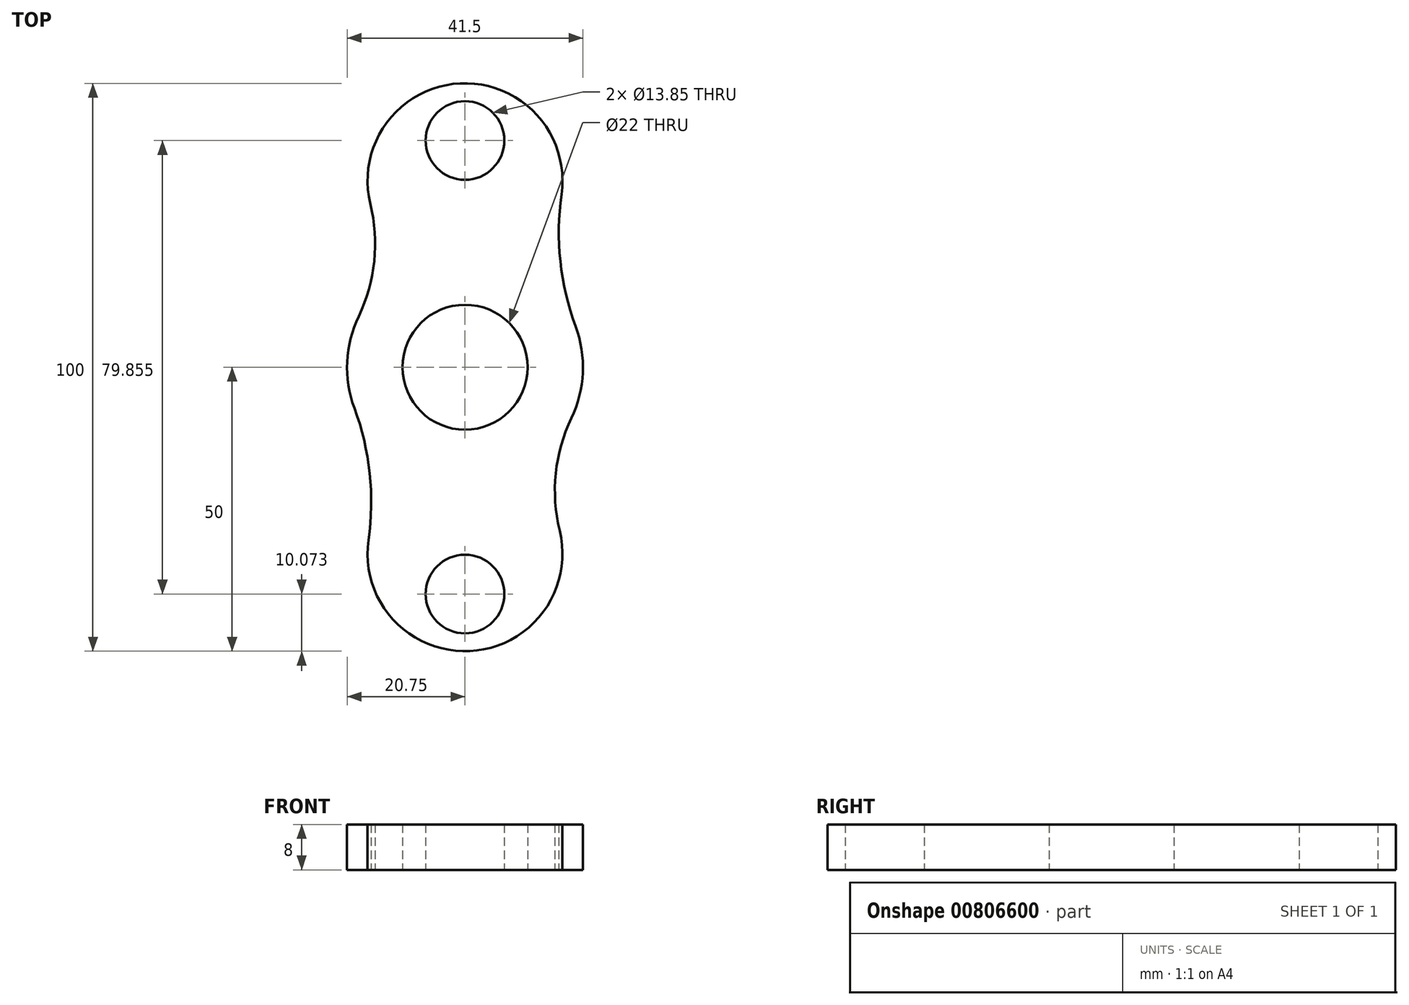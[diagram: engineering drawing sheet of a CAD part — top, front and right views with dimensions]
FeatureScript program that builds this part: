
annotation { "Feature Type Name" : "Feature", "Feature Type Description" : "" }
export const myFeature = defineFeature(function(context is Context, id is Id, definition is map)
    precondition{}
    {
        {
            var Q0;
            Q0=qCreatedBy(makeId("Top.planeOp"),FACE);
            var sketch = newSketch(context, id + "F0", { "sketchPlane" : qUnion([Q0])});
            skCircle(sketch, "E0", {"center": v(0, 0) * mm, "radius": 11 * mm});
            skCircle(sketch, "E1", {"center": v(0, 0) * mm, "radius": 50 * mm, "construction": true});
            skArc(sketch, "E2", {"start": v(16.99, 30.43) * mm, "mid": v(-0.84, 49.98) * mm, "end": v(-16.67, 28.77) * mm});
            skArc(sketch, "E3", {"start": v(-18.72, 8.96) * mm, "mid": v(-20.73, 0.96) * mm, "end": v(-19.47, -7.2) * mm});
            skArc(sketch, "E4", {"start": v(-18.72, 8.96) * mm, "mid": v(-15.98, 18.69) * mm, "end": v(-16.67, 28.77) * mm});
            skArc(sketch, "E5", {"start": v(16.99, 30.43) * mm, "mid": v(16.78, 18.66) * mm, "end": v(19.47, 7.2) * mm});
            skArc(sketch, "E6.1.0", {"start": v(-16.99, -30.43) * mm, "mid": v(-16.78, -18.66) * mm, "end": v(-19.47, -7.2) * mm});
            skArc(sketch, "E6.1.1", {"start": v(-16.99, -30.43) * mm, "mid": v(0.84, -49.98) * mm, "end": v(16.67, -28.77) * mm});
            skArc(sketch, "E6.1.2", {"start": v(18.72, -8.96) * mm, "mid": v(15.98, -18.69) * mm, "end": v(16.67, -28.77) * mm});
            skArc(sketch, "E7.trimOffspring", {"start": v(18.72, -8.96) * mm, "mid": v(20.73, -0.96) * mm, "end": v(19.47, 7.2) * mm});
            skCircle(sketch, "E8", {"center": v(0, 39.93) * mm, "radius": 6.93 * mm});
            skCircle(sketch, "E9.1.0", {"center": v(0, -39.93) * mm, "radius": 6.93 * mm});
            skSolve(sketch);
        }
        {
            var Q0;
            Q0=makeQuery(id+"F0.imprint","IMPRINT",FACE,{"disambiguationData":[TD([[makeQuery(id+"F0.imprint","IMPRINT",EDGE,{"derivedFrom":sQuery(id+"F0.wireOp",EDGE,"E0")}),-1.0]])]});
            extrude(context, id + "F1", {"entities" : qUnion([Q0]), "depth" : 8 * mm, "offsetDistance" : 25 * mm});
        }
    });
